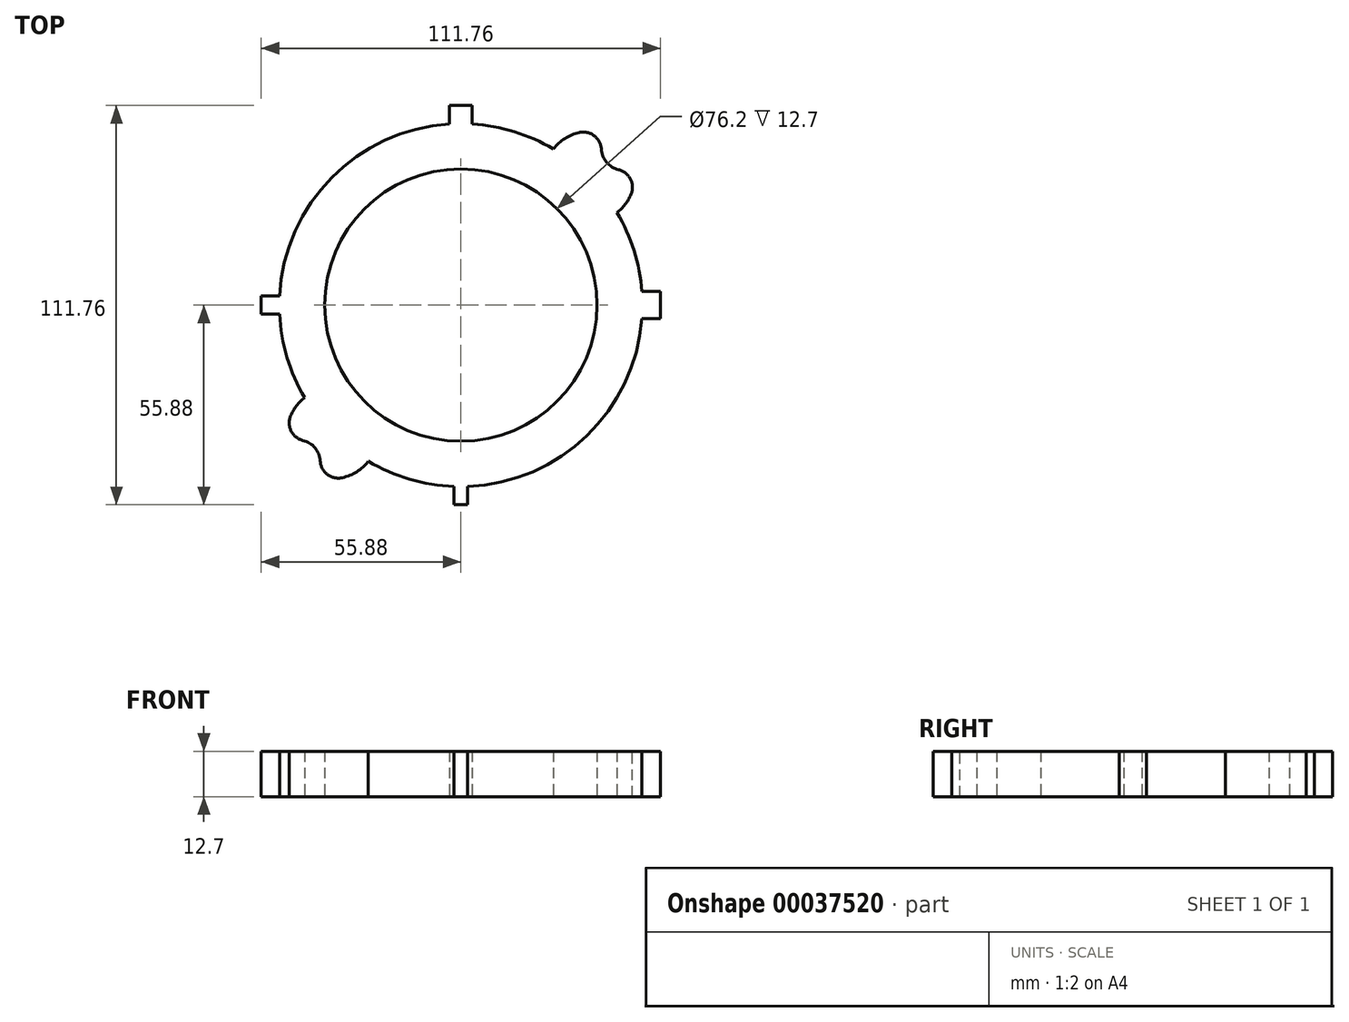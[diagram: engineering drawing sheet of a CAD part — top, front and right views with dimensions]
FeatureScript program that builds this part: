
annotation { "Feature Type Name" : "Feature", "Feature Type Description" : "" }
export const myFeature = defineFeature(function(context is Context, id is Id, definition is map)
    precondition{}
    {
        {
            var Q0;
            Q0=qCreatedBy(makeId("Top.planeOp"),FACE);
            var sketch = newSketch(context, id + "F0", { "sketchPlane" : qUnion([Q0])});
            skCircle(sketch, "E0", {"center": v(0, 0) * mm, "radius": 38.1 * mm});
            skCircle(sketch, "E1", {"center": v(0, 0) * mm, "radius": 50.8 * mm});
            skLineSegment(sketch, "E2.rect.bottom", {"start": v(3.17, 55.88) * mm, "end": v(-3.18, 55.88) * mm});
            skLineSegment(sketch, "E2.rect.left", {"start": v(3.17, 55.88) * mm, "end": v(3.18, 50.7) * mm});
            skLineSegment(sketch, "E2.rect.right", {"start": v(-3.18, 55.88) * mm, "end": v(-3.18, 50.7) * mm});
            skPoint(sketch, "E2.rect.middle", {"position": v(0, 50.8) * mm});
            skLineSegment(sketch, "E3.rect.bottom", {"start": v(-55.88, 2.54) * mm, "end": v(-50.74, 2.54) * mm});
            skLineSegment(sketch, "E3.rect.top", {"start": v(-55.88, -2.54) * mm, "end": v(-50.74, -2.54) * mm});
            skLineSegment(sketch, "E3.rect.left", {"start": v(-55.88, 2.54) * mm, "end": v(-55.88, -2.54) * mm});
            skPoint(sketch, "E3.rect.middle", {"position": v(-50.8, 0) * mm});
            skLineSegment(sketch, "E4.rect.bottom", {"start": v(1.9, -55.88) * mm, "end": v(-1.9, -55.88) * mm});
            skLineSegment(sketch, "E4.rect.left", {"start": v(1.9, -55.88) * mm, "end": v(1.9, -50.76) * mm});
            skLineSegment(sketch, "E4.rect.right", {"start": v(-1.9, -55.88) * mm, "end": v(-1.9, -50.76) * mm});
            skPoint(sketch, "E4.rect.middle", {"position": v(0, -50.8) * mm});
            skLineSegment(sketch, "E5.rect.bottom", {"start": v(55.88, 3.81) * mm, "end": v(50.66, 3.81) * mm});
            skLineSegment(sketch, "E5.rect.top", {"start": v(55.88, -3.8) * mm, "end": v(50.66, -3.8) * mm});
            skLineSegment(sketch, "E5.rect.left", {"start": v(55.88, 3.81) * mm, "end": v(55.88, -3.8) * mm});
            skPoint(sketch, "E5.rect.middle", {"position": v(50.8, 0) * mm});
            skArc(sketch, "E6", {"start": v(43.7, 25.89) * mm, "mid": v(47.8, 31.44) * mm, "end": v(48.4, 38.31) * mm});
            skPoint(sketch, "E3.rect.right.start.orphan", {"position": v(-45.72, 2.54) * mm});
            skPoint(sketch, "E7.orphan", {"position": v(-45.72, -2.54) * mm});
            skPoint(sketch, "E2.rect.top.end.orphan", {"position": v(-3.17, 45.72) * mm});
            skPoint(sketch, "E8.orphan", {"position": v(3.18, 45.72) * mm});
            skPoint(sketch, "E9.orphan", {"position": v(45.72, 3.81) * mm});
            skPoint(sketch, "E10.orphan", {"position": v(45.72, -3.8) * mm});
            skPoint(sketch, "E11.orphan", {"position": v(-1.9, -45.72) * mm});
            skPoint(sketch, "E12.orphan", {"position": v(1.9, -45.72) * mm});
            skArc(sketch, "E13", {"start": v(40.52, 47.76) * mm, "mid": v(40.8, 39.99) * mm, "end": v(48.4, 38.31) * mm});
            skArc(sketch, "E14.trimOffspring", {"start": v(40.52, 47.76) * mm, "mid": v(32.53, 48.16) * mm, "end": v(25.89, 43.7) * mm});
            skArc(sketch, "E15.1.0", {"start": v(-40.52, -47.76) * mm, "mid": v(-32.53, -48.16) * mm, "end": v(-25.89, -43.7) * mm});
            skArc(sketch, "E15.1.1", {"start": v(-40.52, -47.76) * mm, "mid": v(-40.8, -39.99) * mm, "end": v(-48.4, -38.31) * mm});
            skArc(sketch, "E15.1.2", {"start": v(-43.7, -25.89) * mm, "mid": v(-47.8, -31.44) * mm, "end": v(-48.4, -38.31) * mm});
            skSolve(sketch);
        }
        {
            var Q0;
            Q0 = qSketchRegion(id + "F0", true);
            extrude(context, id + "F1", {"entities" : qUnion([Q0]), "depth" : 12.7 * mm});
        }
        {
            var Q0;
            Q0=makeQuery(id+"F1.opExtrude","SWEPT_EDGE",EDGE,{"disambiguationData":[OSD([sQuery(id+"F0.wireOp",EDGE,"E15.1.1"),sQuery(id+"F0.wireOp",EDGE,"E15.1.2")])]});
            var Q1;
            Q1=makeQuery(id+"F1.opExtrude","SWEPT_EDGE",EDGE,{"disambiguationData":[OSD([sQuery(id+"F0.wireOp",EDGE,"E15.1.0"),sQuery(id+"F0.wireOp",EDGE,"E15.1.1")])]});
            var Q2;
            Q2=makeQuery(id+"F1.opExtrude","SWEPT_EDGE",EDGE,{"disambiguationData":[OSD([sQuery(id+"F0.wireOp",EDGE,"E13"),sQuery(id+"F0.wireOp",EDGE,"E14.trimOffspring")])]});
            var Q3;
            Q3=makeQuery(id+"F1.opExtrude","SWEPT_EDGE",EDGE,{"disambiguationData":[OSD([sQuery(id+"F0.wireOp",EDGE,"E6"),sQuery(id+"F0.wireOp",EDGE,"E13")])]});
            fillet(context, id + "F2", {"entities" : qUnion([Q0, Q1, Q2, Q3]), "radius" : 5.08 * mm, "tangentPropagation" : true, "allowEdgeOverflow" : false});
        }
    });
